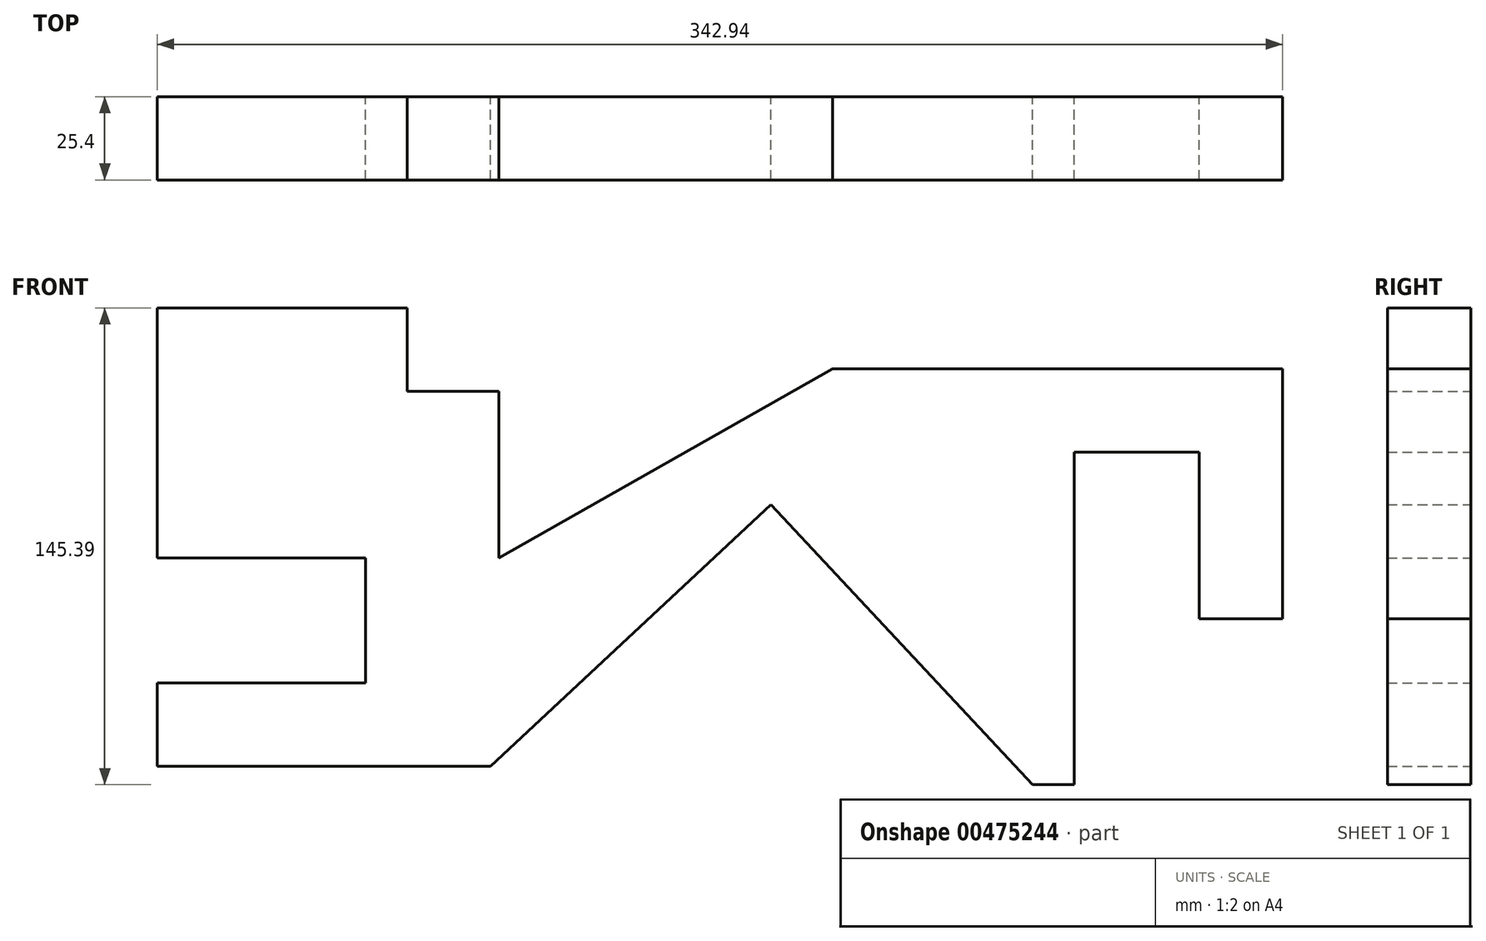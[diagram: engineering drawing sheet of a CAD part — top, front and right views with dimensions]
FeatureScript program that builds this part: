
annotation { "Feature Type Name" : "Feature", "Feature Type Description" : "" }
export const myFeature = defineFeature(function(context is Context, id is Id, definition is map)
    precondition{}
    {
        {
            var Q0;
            Q0=qCreatedBy(makeId("Front.planeOp"),FACE);
            var sketch = newSketch(context, id + "F0", { "sketchPlane" : qUnion([Q0])});
            skLineSegment(sketch, "E0", {"start": v(-63.5, 76.2) * mm, "end": v(-63.5, 0) * mm});
            skLineSegment(sketch, "E1", {"start": v(-63.5, 0) * mm, "end": v(0, 0) * mm});
            skLineSegment(sketch, "E2", {"start": v(0, 0) * mm, "end": v(0, -38.1) * mm});
            skLineSegment(sketch, "E3", {"start": v(0, -38.1) * mm, "end": v(-63.5, -38.1) * mm});
            skLineSegment(sketch, "E4", {"start": v(-63.5, -38.1) * mm, "end": v(-63.5, -63.5) * mm});
            skLineSegment(sketch, "E5", {"start": v(-63.5, -63.5) * mm, "end": v(38.1, -63.5) * mm});
            skPoint(sketch, "E6.end.orphan", {"position": v(70.47, -38.1) * mm});
            skLineSegment(sketch, "E7", {"start": v(38.1, -63.5) * mm, "end": v(123.51, 16.22) * mm});
            skLineSegment(sketch, "E8", {"start": v(123.51, 16.22) * mm, "end": v(203.24, -69.19) * mm});
            skLineSegment(sketch, "E9", {"start": v(203.24, -69.19) * mm, "end": v(215.94, -69.19) * mm});
            skLineSegment(sketch, "E10", {"start": v(215.94, -69.19) * mm, "end": v(215.94, 32.23) * mm});
            skLineSegment(sketch, "E11", {"start": v(215.94, 32.23) * mm, "end": v(254.04, 32.23) * mm});
            skLineSegment(sketch, "E12", {"start": v(254.04, 32.23) * mm, "end": v(254.04, -18.57) * mm});
            skLineSegment(sketch, "E13", {"start": v(254.04, -18.57) * mm, "end": v(279.44, -18.57) * mm});
            skPoint(sketch, "E14.end.orphan", {"position": v(219.79, 32.23) * mm});
            skLineSegment(sketch, "E15", {"start": v(279.44, -18.57) * mm, "end": v(279.44, 57.63) * mm});
            skLineSegment(sketch, "E16", {"start": v(279.44, 57.63) * mm, "end": v(142.28, 57.63) * mm});
            skLineSegment(sketch, "E17", {"start": v(142.28, 57.63) * mm, "end": v(40.64, 0) * mm});
            skLineSegment(sketch, "E18", {"start": v(40.64, 0) * mm, "end": v(40.64, 50.8) * mm});
            skLineSegment(sketch, "E19", {"start": v(40.64, 50.8) * mm, "end": v(12.7, 50.8) * mm});
            skLineSegment(sketch, "E20", {"start": v(12.7, 50.8) * mm, "end": v(12.7, 76.2) * mm});
            skLineSegment(sketch, "E21", {"start": v(12.7, 76.2) * mm, "end": v(-63.5, 76.2) * mm});
            skPoint(sketch, "E22.end.orphan", {"position": v(-63.5, 116.44) * mm});
            skLineSegment(sketch, "E23", {"start": v(-63.5, 76.2) * mm, "end": v(-63.5, 76.2) * mm});
            skSolve(sketch);
        }
        {
            var Q0;
            Q0 = qSketchRegion(id + "F0", true);
            extrude(context, id + "F1", {"entities" : qUnion([Q0]), "depth" : 25.4 * mm});
        }
    });
